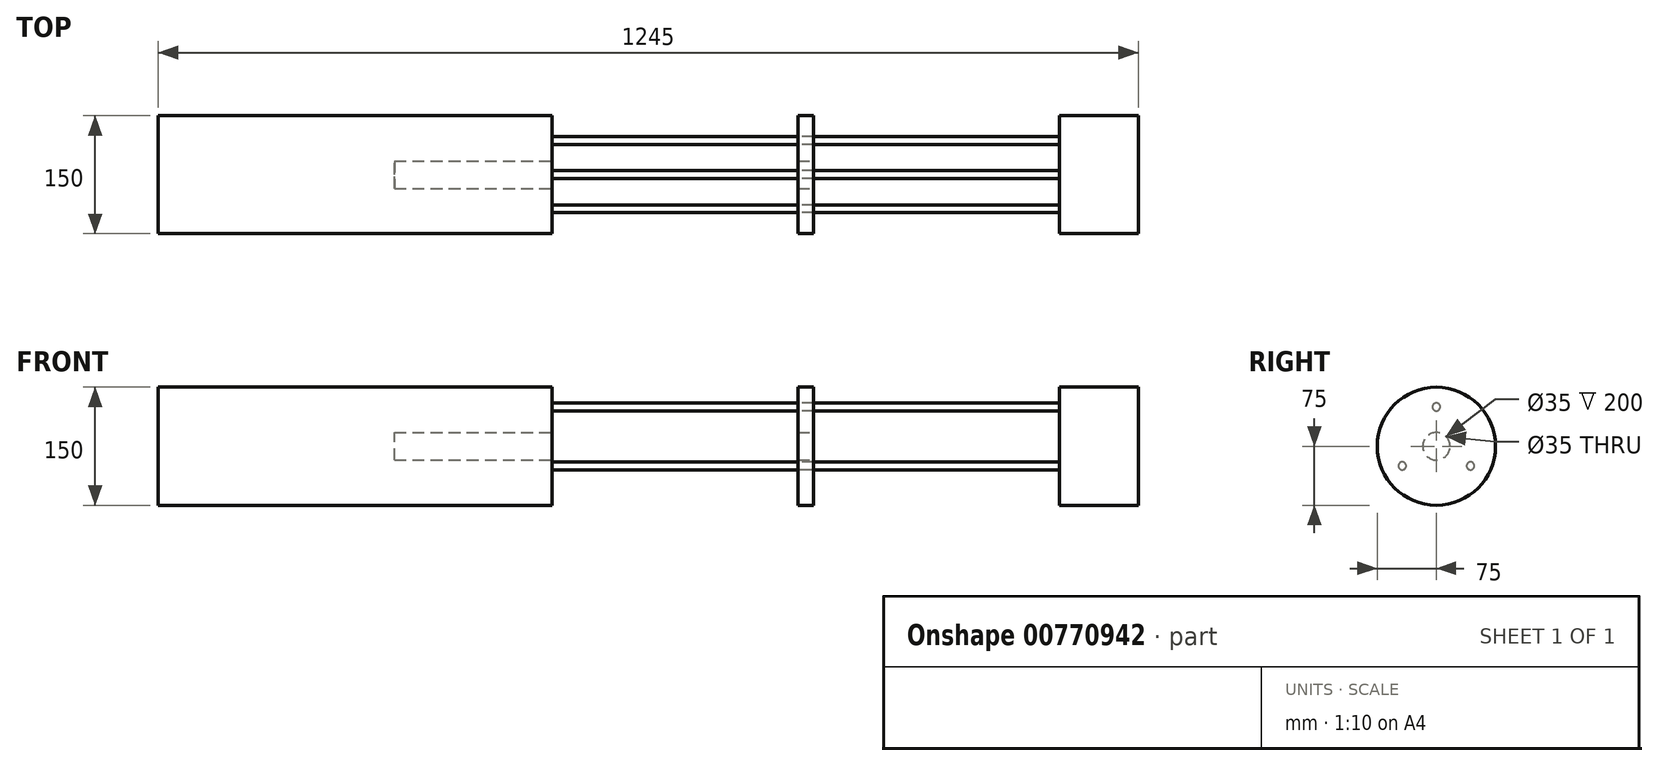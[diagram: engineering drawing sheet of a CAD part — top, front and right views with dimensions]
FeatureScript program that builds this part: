
annotation { "Feature Type Name" : "Feature", "Feature Type Description" : "" }
export const myFeature = defineFeature(function(context is Context, id is Id, definition is map)
    precondition{}
    {
        {
            var Q0;
            Q0=qCreatedBy(makeId("Top.planeOp"),FACE);
            var sketch = newSketch(context, id + "F0", { "sketchPlane" : qUnion([Q0])});
            skLineSegment(sketch, "E0", {"start": v(-500, 0) * mm, "end": v(-500, -75) * mm});
            skLineSegment(sketch, "E1", {"start": v(-500, -75) * mm, "end": v(0, -75) * mm});
            skLineSegment(sketch, "E2", {"start": v(0, -75) * mm, "end": v(0, -17.5) * mm});
            skLineSegment(sketch, "E3", {"start": v(0, -17.5) * mm, "end": v(-200, -17.5) * mm});
            skLineSegment(sketch, "E4", {"start": v(-200, -17.5) * mm, "end": v(-200, 0) * mm});
            skLineSegment(sketch, "E5", {"start": v(-200, 0) * mm, "end": v(-500, 0) * mm});
            skSolve(sketch);
        }
        {
            var Q0;
            Q0=qCreatedBy(makeId("Top.planeOp"),FACE);
            var sketch = newSketch(context, id + "F1", { "sketchPlane" : qUnion([Q0])});
            skLineSegment(sketch, "E6.bottom", {"start": v(645, -75) * mm, "end": v(745, -75) * mm});
            skLineSegment(sketch, "E6.top", {"start": v(645, 0) * mm, "end": v(745, 0) * mm});
            skLineSegment(sketch, "E6.left", {"start": v(645, -75) * mm, "end": v(645, 0) * mm});
            skLineSegment(sketch, "E6.right", {"start": v(745, -75) * mm, "end": v(745, 0) * mm});
            skSolve(sketch);
        }
        {
            var Q0;
            Q0=qCreatedBy(makeId("Top.planeOp"),FACE);
            var sketch = newSketch(context, id + "F2", { "sketchPlane" : qUnion([Q0])});
            skLineSegment(sketch, "E7.bottom", {"start": v(312.5, -17.5) * mm, "end": v(332.5, -17.5) * mm});
            skLineSegment(sketch, "E7.top", {"start": v(312.5, -75) * mm, "end": v(332.5, -75) * mm});
            skLineSegment(sketch, "E7.left", {"start": v(312.5, -17.5) * mm, "end": v(312.5, -75) * mm});
            skLineSegment(sketch, "E7.right", {"start": v(332.5, -17.5) * mm, "end": v(332.5, -75) * mm});
            skSolve(sketch);
        }
        {
            var Q0;
            Q0=makeQuery(id+"F0.imprint","IMPRINT",FACE,{"disambiguationData":[TD([[makeQuery(id+"F0.imprint","IMPRINT",EDGE,{"derivedFrom":sQuery(id+"F0.wireOp",EDGE,"E0")}),1.0]])]});
            var Q1;
            Q1=makeQuery(id+"F2.imprint","IMPRINT",FACE,{"disambiguationData":[TD([[makeQuery(id+"F2.imprint","IMPRINT",EDGE,{"derivedFrom":sQuery(id+"F2.wireOp",EDGE,"00949d21-04e9-4acd-8803-175544acd0f4.4.0.0")}),1.0]])]});
            var Q2;
            Q2=makeQuery(id+"F2.imprint","IMPRINT",FACE,{"disambiguationData":[TD([[makeQuery(id+"F2.imprint","IMPRINT",EDGE,{"derivedFrom":sQuery(id+"F2.wireOp",EDGE,"00949d21-04e9-4acd-8803-175544acd0f4.9.0.0")}),1.0]])]});
            var Q3;
            Q3=makeQuery(id+"F2.imprint","IMPRINT",FACE,{"disambiguationData":[TD([[makeQuery(id+"F2.imprint","IMPRINT",EDGE,{"derivedFrom":sQuery(id+"F2.wireOp",EDGE,"00949d21-04e9-4acd-8803-175544acd0f4.3.0.0")}),1.0]])]});
            var Q4;
            Q4=makeQuery(id+"F2.imprint","IMPRINT",FACE,{"disambiguationData":[TD([[makeQuery(id+"F2.imprint","IMPRINT",EDGE,{"derivedFrom":sQuery(id+"F2.wireOp",EDGE,"00949d21-04e9-4acd-8803-175544acd0f4.2.0.0")}),1.0]])]});
            var Q5;
            Q5=makeQuery(id+"F2.imprint","IMPRINT",FACE,{"disambiguationData":[TD([[makeQuery(id+"F2.imprint","IMPRINT",EDGE,{"derivedFrom":sQuery(id+"F2.wireOp",EDGE,"00949d21-04e9-4acd-8803-175544acd0f4.10.0.0")}),1.0]])]});
            var Q6;
            Q6=makeQuery(id+"F2.imprint","IMPRINT",FACE,{"disambiguationData":[TD([[makeQuery(id+"F2.imprint","IMPRINT",EDGE,{"derivedFrom":sQuery(id+"F2.wireOp",EDGE,"00949d21-04e9-4acd-8803-175544acd0f4.1.0.0")}),1.0]])]});
            var Q7;
            Q7=makeQuery(id+"F2.imprint","IMPRINT",FACE,{"disambiguationData":[TD([[makeQuery(id+"F2.imprint","IMPRINT",EDGE,{"derivedFrom":sQuery(id+"F2.wireOp",EDGE,"00949d21-04e9-4acd-8803-175544acd0f4.8.0.0")}),1.0]])]});
            var Q8;
            Q8=makeQuery(id+"F2.imprint","IMPRINT",FACE,{"disambiguationData":[TD([[makeQuery(id+"F2.imprint","IMPRINT",EDGE,{"derivedFrom":sQuery(id+"F2.wireOp",EDGE,"00949d21-04e9-4acd-8803-175544acd0f4.17.0.0")}),1.0]])]});
            var Q9;
            Q9=makeQuery(id+"F2.imprint","IMPRINT",FACE,{"disambiguationData":[TD([[makeQuery(id+"F2.imprint","IMPRINT",EDGE,{"derivedFrom":sQuery(id+"F2.wireOp",EDGE,"00949d21-04e9-4acd-8803-175544acd0f4.16.0.0")}),1.0]])]});
            var Q10;
            Q10=makeQuery(id+"F2.imprint","IMPRINT",FACE,{"disambiguationData":[TD([[makeQuery(id+"F2.imprint","IMPRINT",EDGE,{"derivedFrom":sQuery(id+"F2.wireOp",EDGE,"00949d21-04e9-4acd-8803-175544acd0f4.12.0.0")}),1.0]])]});
            var Q11;
            Q11=makeQuery(id+"F2.imprint","IMPRINT",FACE,{"disambiguationData":[TD([[makeQuery(id+"F2.imprint","IMPRINT",EDGE,{"derivedFrom":sQuery(id+"F2.wireOp",EDGE,"00949d21-04e9-4acd-8803-175544acd0f4.5.0.0")}),1.0]])]});
            var Q12;
            Q12=makeQuery(id+"F2.imprint","IMPRINT",FACE,{"disambiguationData":[TD([[makeQuery(id+"F2.imprint","IMPRINT",EDGE,{"derivedFrom":sQuery(id+"F2.wireOp",EDGE,"00949d21-04e9-4acd-8803-175544acd0f4.6.0.0")}),1.0]])]});
            var Q13;
            Q13=makeQuery(id+"F2.imprint","IMPRINT",FACE,{"disambiguationData":[TD([[makeQuery(id+"F2.imprint","IMPRINT",EDGE,{"derivedFrom":sQuery(id+"F2.wireOp",EDGE,"00949d21-04e9-4acd-8803-175544acd0f4.11.0.0")}),1.0]])]});
            var Q14;
            Q14=makeQuery(id+"F2.imprint","IMPRINT",FACE,{"disambiguationData":[TD([[makeQuery(id+"F2.imprint","IMPRINT",EDGE,{"derivedFrom":sQuery(id+"F2.wireOp",EDGE,"00949d21-04e9-4acd-8803-175544acd0f4.7.0.0")}),1.0]])]});
            var Q15;
            Q15=makeQuery(id+"F2.imprint","IMPRINT",FACE,{"disambiguationData":[TD([[makeQuery(id+"F2.imprint","IMPRINT",EDGE,{"derivedFrom":sQuery(id+"F2.wireOp",EDGE,"E7.bottom")}),-1.0]])]});
            var Q16;
            Q16=makeQuery(id+"F2.imprint","IMPRINT",FACE,{"disambiguationData":[TD([[makeQuery(id+"F2.imprint","IMPRINT",EDGE,{"derivedFrom":sQuery(id+"F2.wireOp",EDGE,"00949d21-04e9-4acd-8803-175544acd0f4.14.0.0")}),1.0]])]});
            var Q17;
            Q17=makeQuery(id+"F2.imprint","IMPRINT",FACE,{"disambiguationData":[TD([[makeQuery(id+"F2.imprint","IMPRINT",EDGE,{"derivedFrom":sQuery(id+"F2.wireOp",EDGE,"00949d21-04e9-4acd-8803-175544acd0f4.13.0.0")}),1.0]])]});
            var Q18;
            Q18=makeQuery(id+"F1.imprint","IMPRINT",FACE,{"disambiguationData":[TD([[makeQuery(id+"F1.imprint","IMPRINT",EDGE,{"derivedFrom":sQuery(id+"F1.wireOp",EDGE,"E6.bottom")}),1.0]])]});
            var Q19;
            Q19=makeQuery(id+"F2.imprint","IMPRINT",FACE,{"disambiguationData":[TD([[makeQuery(id+"F2.imprint","IMPRINT",EDGE,{"derivedFrom":sQuery(id+"F2.wireOp",EDGE,"00949d21-04e9-4acd-8803-175544acd0f4.15.0.0")}),1.0]])]});
            var Q20;
            Q20=sQuery(id+"F0.wireOp",EDGE,"E5");
            revolve(context, id + "F3", {"surfaceOperationType" : NewSurfaceOperationType.NEW, "entities" : qUnion([Q0, Q1, Q2, Q3, Q4, Q5, Q6, Q7, Q8, Q9, Q10, Q11, Q12, Q13, Q14, Q15, Q16, Q17, Q18, Q19]), "axis" : qUnion([Q20]), "revolveType" : RevolveType.FULL});
        }
        {
            var Q0;
            Q0=qCreatedBy(makeId("Right.planeOp"),FACE);
            var sketch = newSketch(context, id + "F4", { "sketchPlane" : qUnion([Q0])});
            skCircle(sketch, "E8", {"center": v(0, 50) * mm, "radius": 5 * mm});
            skCircle(sketch, "E9.1.0", {"center": v(-43.3, -25) * mm, "radius": 5 * mm});
            skCircle(sketch, "E9.2.0", {"center": v(43.3, -25) * mm, "radius": 5 * mm});
            skPoint(sketch, "E9.center", {"position": v(0, 0) * mm});
            skSolve(sketch);
        }
        {
            var Q0;
            Q0=qSketchRegion(id+"F4",true);
            var Q1;
            Q1=makeQuery(id+"F3.opRevolve","SWEPT_FACE",FACE,{"disambiguationData":[OSD([sQuery(id+"F1.wireOp",EDGE,"E6.left")])]});
            extrude(context, id + "F5", {"entities" : qUnion([Q0]), "endBound" : BoundingType.UP_TO_SURFACE, "depth" : 25 * mm, "endBoundEntityFace" : qUnion([Q1]), "offsetDistance" : 25 * mm, "offsetOppositeDirection" : true});
        }
    });
